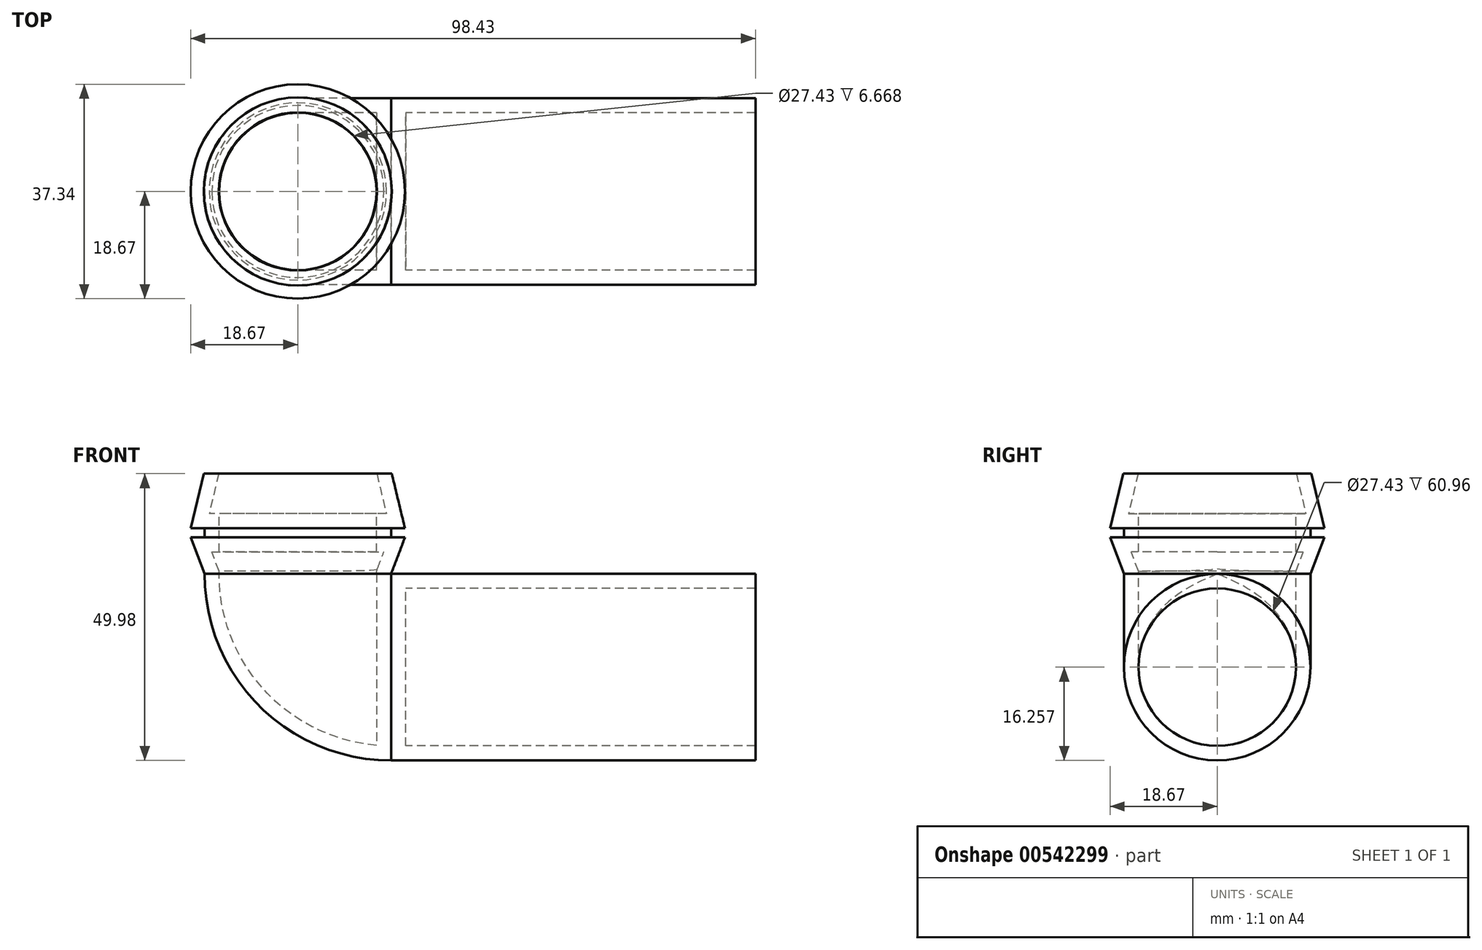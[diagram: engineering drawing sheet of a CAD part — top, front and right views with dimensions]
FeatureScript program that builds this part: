
annotation { "Feature Type Name" : "Feature", "Feature Type Description" : "" }
export const myFeature = defineFeature(function(context is Context, id is Id, definition is map)
    precondition{}
    {
        {
            var Q0;
            Q0=qCreatedBy(makeId("Top.planeOp"),FACE);
            var sketch = newSketch(context, id + "F0", { "sketchPlane" : qUnion([Q0])});
            skCircle(sketch, "E0", {"center": v(0, 0) * mm, "radius": 18.67 * mm});
            skSolve(sketch);
        }
        {
            var Q0;
            Q0=qCreatedBy(makeId("Top.planeOp"),FACE);
            cPlane(context, id + "F1", {"entities" : qUnion([Q0]), "cplaneType" : CPlaneType.OFFSET, "offset" : 9.52 * mm, "width" : 152.4 * mm, "height" : 152.4 * mm});
        }
        {
            var Q0;
            Q0=qCreatedBy(id+"F1.planeOp",FACE);
            var sketch = newSketch(context, id + "F2", { "sketchPlane" : qUnion([Q0])});
            skCircle(sketch, "E1", {"center": v(0, 0) * mm, "radius": 16.38 * mm});
            skSolve(sketch);
        }
        {
            var Q0;
            Q0=makeQuery(id+"F2.imprint","IMPRINT",FACE,{"disambiguationData":[TD([[makeQuery(id+"F2.imprint","IMPRINT",EDGE,{"derivedFrom":sQuery(id+"F2.wireOp",EDGE,"E1")}),1.0]])]});
            var Q1;
            Q1=makeQuery(id+"F0.imprint","IMPRINT",FACE,{"disambiguationData":[TD([[makeQuery(id+"F0.imprint","IMPRINT",EDGE,{"derivedFrom":sQuery(id+"F0.wireOp",EDGE,"E0")}),1.0]])]});
            loft(context, id + "F3", {"sheetProfilesArray" : [{ "sheetProfileEntities" : qUnion([Q0]) }, { "sheetProfileEntities" : qUnion([Q1]) }]});
        }
        {
            var Q0;
            Q0=qCreatedBy(makeId("Top.planeOp"),FACE);
            var sketch = newSketch(context, id + "F4", { "sketchPlane" : qUnion([Q0])});
            skCircle(sketch, "E2", {"center": v(0, 0) * mm, "radius": 16.26 * mm});
            skSolve(sketch);
        }
        {
            var Q0;
            Q0 = qSketchRegion(id + "F4", true);
            extrude(context, id + "F5", {"entities" : qUnion([Q0]), "operationType" : NewBodyOperationType.ADD, "oppositeDirection" : true, "depth" : 1.59 * mm, "offsetDistance" : 25.4 * mm});
        }
        {
            var Q0;
            Q0=makeQuery(id+"F5.opExtrude","CAP_FACE",FACE,{"disambiguationData":[OSD([sQuery(id+"F4.wireOp",EDGE,"E2")])],"isStart":false});
            cPlane(context, id + "F6", {"entities" : qUnion([Q0]), "cplaneType" : CPlaneType.OFFSET, "offset" : 0 * mm, "width" : 152.4 * mm, "height" : 152.4 * mm});
        }
        {
            var Q0;
            Q0=qCreatedBy(id+"F6.planeOp",FACE);
            var sketch = newSketch(context, id + "F7", { "sketchPlane" : qUnion([Q0])});
            skCircle(sketch, "E3", {"center": v(0, 0) * mm, "radius": 18.67 * mm});
            skSolve(sketch);
        }
        {
            var Q0;
            Q0=qCreatedBy(id+"F6.planeOp",FACE);
            var Q1;
            Q1 = qBodyType(qCreatedBy(id + "F9" ,EDGE), BodyType.WIRE);
            cPlane(context, id + "F8", {"entities" : qUnion([Q0, Q1]), "cplaneType" : CPlaneType.OFFSET, "offset" : 6.35 * mm, "width" : 152.4 * mm, "height" : 152.4 * mm});
        }
        {
            var Q0;
            Q0=qCreatedBy(id+"F8.planeOp",FACE);
            var sketch = newSketch(context, id + "F9", { "sketchPlane" : qUnion([Q0])});
            skCircle(sketch, "E4", {"center": v(0, 0) * mm, "radius": 16.26 * mm});
            skLineSegment(sketch, "E5", {"start": v(16.26, 0) * mm, "end": v(16.26, -43.83) * mm, "construction": true});
            skLineSegment(sketch, "E6", {"start": v(16.26, -43.83) * mm, "end": v(16.26, 31.55) * mm, "construction": true});
            skSolve(sketch);
        }
        {
            var Q1;
            Q1=makeQuery(id+"F9.imprint","IMPRINT",FACE,{"disambiguationData":[TD([[makeQuery(id+"F9.imprint","IMPRINT",EDGE,{"derivedFrom":sQuery(id+"F9.wireOp",EDGE,"E4")}),1.0]])]});
            var Q2;
            Q2=makeQuery(id+"F7.imprint","IMPRINT",FACE,{"disambiguationData":[TD([[makeQuery(id+"F7.imprint","IMPRINT",EDGE,{"derivedFrom":sQuery(id+"F7.wireOp",EDGE,"E3")}),1.0]])]});
            loft(context, id + "F10", {"operationType" : NewBodyOperationType.ADD, "sheetProfilesArray" : [{ "sheetProfileEntities" : qUnion([Q1]) }, { "sheetProfileEntities" : qUnion([Q2]) }]});
        }
        {
            var Q0;
            Q0=makeQuery(id+"F9.imprint","IMPRINT",FACE,{"disambiguationData":[TD([[makeQuery(id+"F9.imprint","IMPRINT",EDGE,{"derivedFrom":sQuery(id+"F9.wireOp",EDGE,"E4")}),1.0]])]});
            var Q1;
            Q1=sQuery(id+"F9.wireOp",EDGE,"E6");
            revolve(context, id + "F11", {"operationType" : NewBodyOperationType.ADD, "entities" : qUnion([Q0]), "axis" : qUnion([Q1]), "revolveType" : RevolveType.ONE_DIRECTION, "angle" : 90 * degree});
        }
        {
            var Q0;
            Q0=makeQuery(id+"F11.opRevolve","CAP_FACE",FACE,{"disambiguationData":[OSD([sQuery(id+"F9.wireOp",EDGE,"E4")])],"isStart":false});
            cPlane(context, id + "F12", {"entities" : qUnion([Q0]), "cplaneType" : CPlaneType.OFFSET, "offset" : 0 * mm, "width" : 152.4 * mm, "height" : 152.4 * mm});
        }
        {
            var Q0;
            Q0=makeQuery(id+"F11.opRevolve","CAP_FACE",FACE,{"disambiguationData":[OSD([sQuery(id+"F9.wireOp",EDGE,"E4")])],"isStart":false});
            extrude(context, id + "F13", {"entities" : qUnion([Q0]), "depth" : 63.5 * mm, "offsetDistance" : 25.4 * mm});
        }
        {
            var Q0;
            Q0=makeQuery(id+"F3.opLoft","CAP_FACE",FACE,{"disambiguationData":[OSD([makeQuery(id+"F2.imprint","IMPRINT",FACE,{"disambiguationData":[TD([[makeQuery(id+"F2.imprint","IMPRINT",EDGE,{"derivedFrom":sQuery(id+"F2.wireOp",EDGE,"E1")}),1.0]])]})])],"isStart":true});
            var Q1;
            Q1=makeQuery(id+"F13.opExtrude","CAP_FACE",FACE,{"disambiguationData":[OSD([sQuery(id+"F9.wireOp",EDGE,"E4")])],"isStart":false});
            shell(context, id + "F14", {"entities" : qUnion([Q0, Q1]), "thickness" : 2.54 * mm});
        }
    });
